# Revit family: Gira_540000rfa
name_source: partatom
category: Allgemeines Modell
revit_build: Autodesk Revit 2017 (Build: 20160225_1515(x64)
units: mm (PartAtom-declared; Revit-internal decimal feet)

## family parameters
Basisbauteil = Fläche
Beim Laden mit Abzugskörper schneiden = Nein
Bemaßung runder Anschluss = Durchmesser verwenden
Gemeinsam genutzt = Nein
Kann Basisbauteil für Bewehrung sein = Nein
Raumberechnungspunkt = Nein
Teiletyp = Normal

## types (1)
- Gira_540000rfa
    App control via Bluetooth = Nein
    Applicable with button = Nein
    Applicable with infrared button = Nein
    Applicable with movement sensor = Nein
    Applicable with presence indicator = Nein
    Applicable with time switch/timer = Nein
    Applicable with transmission button = Nein
    Assembly arrangement = Basic element
    BIM = https://media.stage.bim.site
    Beschreibung = S3000 Uni.LED dimm.ins.Std Ins.,System 3000 universal LED dimming insert Standard,,,Features:,- Switching and dimming light bulbs, HV halogen lamps, electronic transformers for halogen or LED lamps, dimmable inductive transformers for halogen or LED lamps, HV LED or compact fluorescent lamps.,- Automatic or manual setting of dimming principle according to load (leading or trailing edge).,- Display of the selected operating mode using LED.,- Bulb-saving switch-on.,- Switch-on brightness can be saved permanently.,- Switch on with the last brightness set, or a saved switch-on brightness.,- Minimum brightness can be set.,- Electronic short-circuit protection.,- Electronic excess-temperature protection.,- Operation with and without neutral conductor connection.,,Notes :,- In general, operating the dimmer without connecting a neutral conductor is possible, although some LED and CFLi light sources require the neutral conductor connection to prevent flickering.,- For operation without a neutral conductor, the minimum load for light bulbs, HV halogen lamps, Gira Tronic transformers, and wound transformers increases to 50 W.,- Electronic transformers and ballast devices for LED lamps can be operated with the dimming procedure stated by the manufacturer.,- If the ambient temperature is higher than 25 C, the connected load must be reduced.
    Category = Other
    Colour = Other
    Connection type = Screwed terminal
    Data sheet = https://katalog.gira.de
    Degree of protection (IP) = IP20
    Dimming phase cut-off = Ja
    Dimming phase cut-on = Ja
    Frequency [Hz] = [50:60]
    GTIN = 4010337047995
    HAN = 540000
    Halogen free = Nein
    Hersteller = Gira
    Integrated timer = Nein
    Light value memory = Ja
    Material = Other
    Material quality = Other
    Max. switching power [Voltampere] = 1000
    Mechanical coding = Nein
    Method of operation = Turn/push button
    Model = Loop-through socket
    Mounting method = Flush mounted (plaster)
    Mounting method shielding connection = Screw
    Nominal voltage [Volt] = 230
    Nominal voltage [Volt] 2 = [230:230]
    Productwebsite = http://katalog.gira.de
    Random generator = Nein
    Separate strain relief = Ja
    Serial dimmer = Nein
    Shielded buses = Ja
    Shielded housing = Nein
    Substation input = Nein
    Suitable for degree of protection (IP) = IP20
    Suitable for rain sensor = Nein
    Suitable for wind sensor = Nein
    Surface finishing = Not applicable
    Surface protection = Other
    Switch-off protection = Nein
    Through loss at 2150 MHz [B] = 0.1
    Through loss at 860 MHz [B] = 0.1
    Transparent = Nein
    Type of fastening = Mounting with claw and screw
    Type of load = Universal and LED Retrofit
    Typname = S3000 uni.LED dimm.ins. Standard Insert
    URL = https://www.gira.de
    Vorgabe-Ansicht = 1219 mm
    With Astro program = Nein
    With brightness sensor connection = Nein
    With glass breaking detector connection = Nein
    With memory function = Nein

## geometry (parser evidence)
native form markers: Sweep x2
no freeform markers — native parametric forms only
